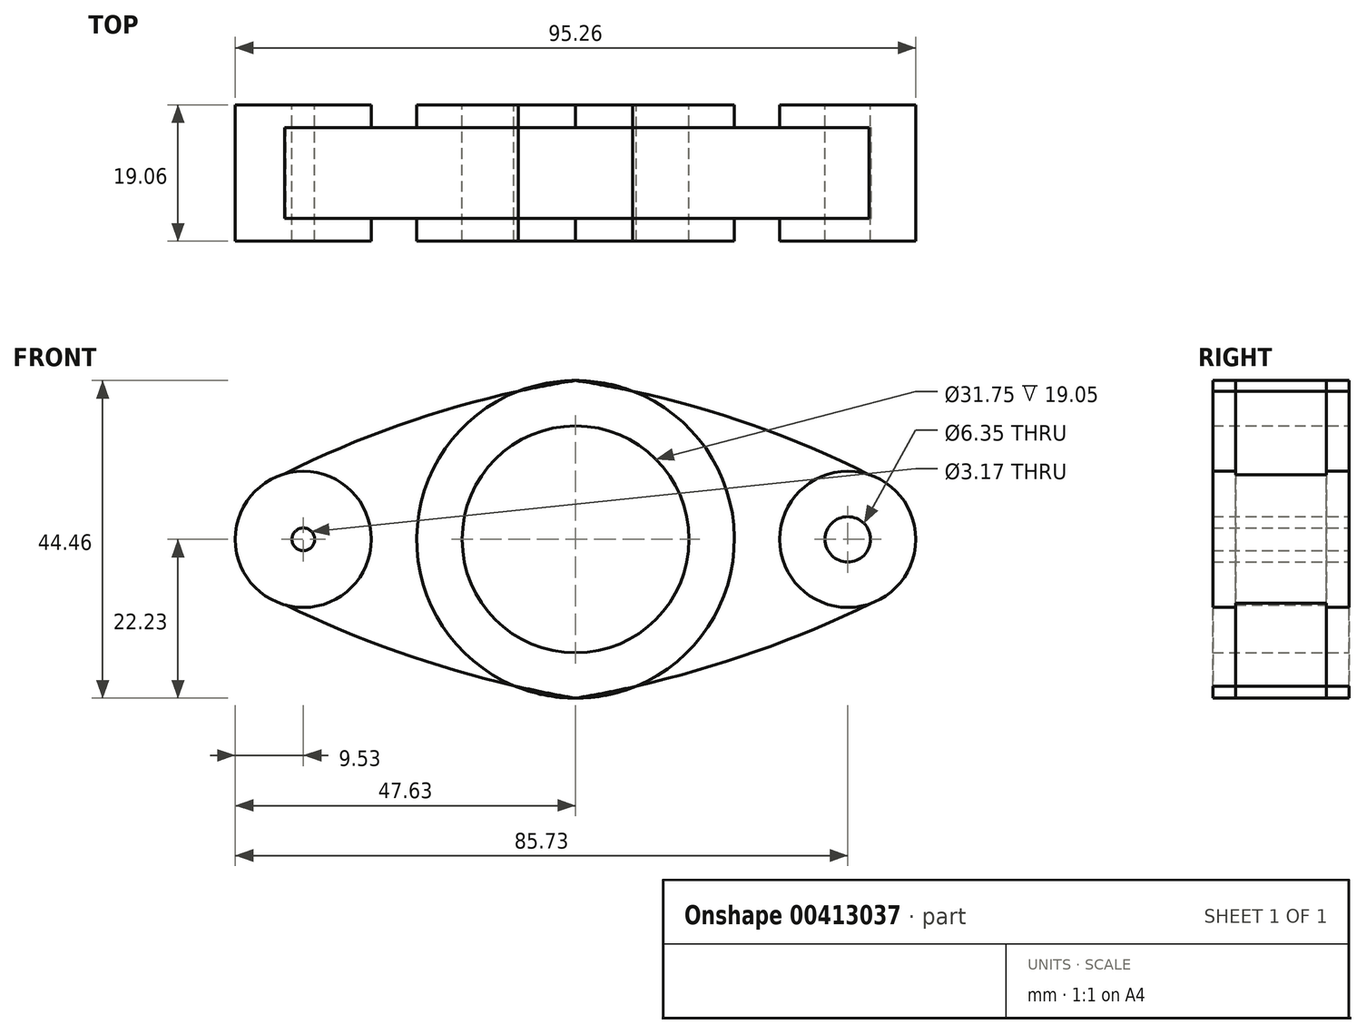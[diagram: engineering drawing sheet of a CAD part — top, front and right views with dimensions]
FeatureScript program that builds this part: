
annotation { "Feature Type Name" : "Feature", "Feature Type Description" : "" }
export const myFeature = defineFeature(function(context is Context, id is Id, definition is map)
    precondition{}
    {
        {
            var Q0;
            Q0=qCreatedBy(makeId("Front.planeOp"),FACE);
            var sketch = newSketch(context, id + "F0", { "sketchPlane" : qUnion([Q0])});
            skCircle(sketch, "E0", {"center": v(0, 0) * mm, "radius": 22.23 * mm});
            skCircle(sketch, "E1", {"center": v(38.1, 0) * mm, "radius": 9.53 * mm});
            skCircle(sketch, "E2", {"center": v(-38.1, 0) * mm, "radius": 9.53 * mm});
            skArc(sketch, "E3", {"start": v(0, 22.22) * mm, "mid": v(-20.88, 17.27) * mm, "end": v(-40.74, 9.15) * mm});
            skArc(sketch, "E4", {"start": v(-40.55, -9.2) * mm, "mid": v(-20.73, -17.14) * mm, "end": v(0, -22.23) * mm});
            skArc(sketch, "E5", {"start": v(0, -22.23) * mm, "mid": v(21.18, -17.06) * mm, "end": v(41.41, -8.93) * mm});
            skArc(sketch, "E6", {"start": v(41.04, 9.06) * mm, "mid": v(21.04, 17.24) * mm, "end": v(0, 22.22) * mm});
            skCircle(sketch, "E7", {"center": v(0, 0) * mm, "radius": 15.88 * mm});
            skCircle(sketch, "E8", {"center": v(38.1, 0) * mm, "radius": 3.18 * mm});
            skCircle(sketch, "E9", {"center": v(-38.1, 0) * mm, "radius": 1.59 * mm});
            skSolve(sketch);
        }
        {
            var Q0;
            Q0 = qSketchRegion(id + "F0", true);
            extrude(context, id + "F1", {"entities" : qUnion([Q0]), "depth" : 6.35 * mm, "hasSecondDirection" : true, "secondDirectionOppositeDirection" : true, "secondDirectionDepth" : 6.35 * mm});
        }
        {
            var Q0;
            Q0=makeQuery(id+"F0.imprint","IMPRINT",FACE,{"disambiguationData":[TD([[makeQuery(id+"F0.imprint","IMPRINT",EDGE,{"derivedFrom":sQuery(id+"F0.wireOp",EDGE,"E8")}),-1.0]])]});
            var Q1;
            Q1=makeQuery(id+"F0.imprint","IMPRINT",FACE,{"disambiguationData":[TD([[makeQuery(id+"F0.imprint","IMPRINT",EDGE,{"derivedFrom":sQuery(id+"F0.wireOp",EDGE,"E9")}),-1.0]])]});
            var Q2;
            Q2=makeQuery(id+"F0.imprint","IMPRINT",FACE,{"disambiguationData":[TD([[makeQuery(id+"F0.imprint","IMPRINT",EDGE,{"derivedFrom":sQuery(id+"F0.wireOp",EDGE,"E7")}),-1.0]])]});
            extrude(context, id + "F2", {"entities" : qUnion([Q0, Q1, Q2]), "operationType" : NewBodyOperationType.ADD, "depth" : 9.52 * mm, "hasSecondDirection" : true, "secondDirectionOppositeDirection" : true, "secondDirectionDepth" : 9.52 * mm});
        }
    });
